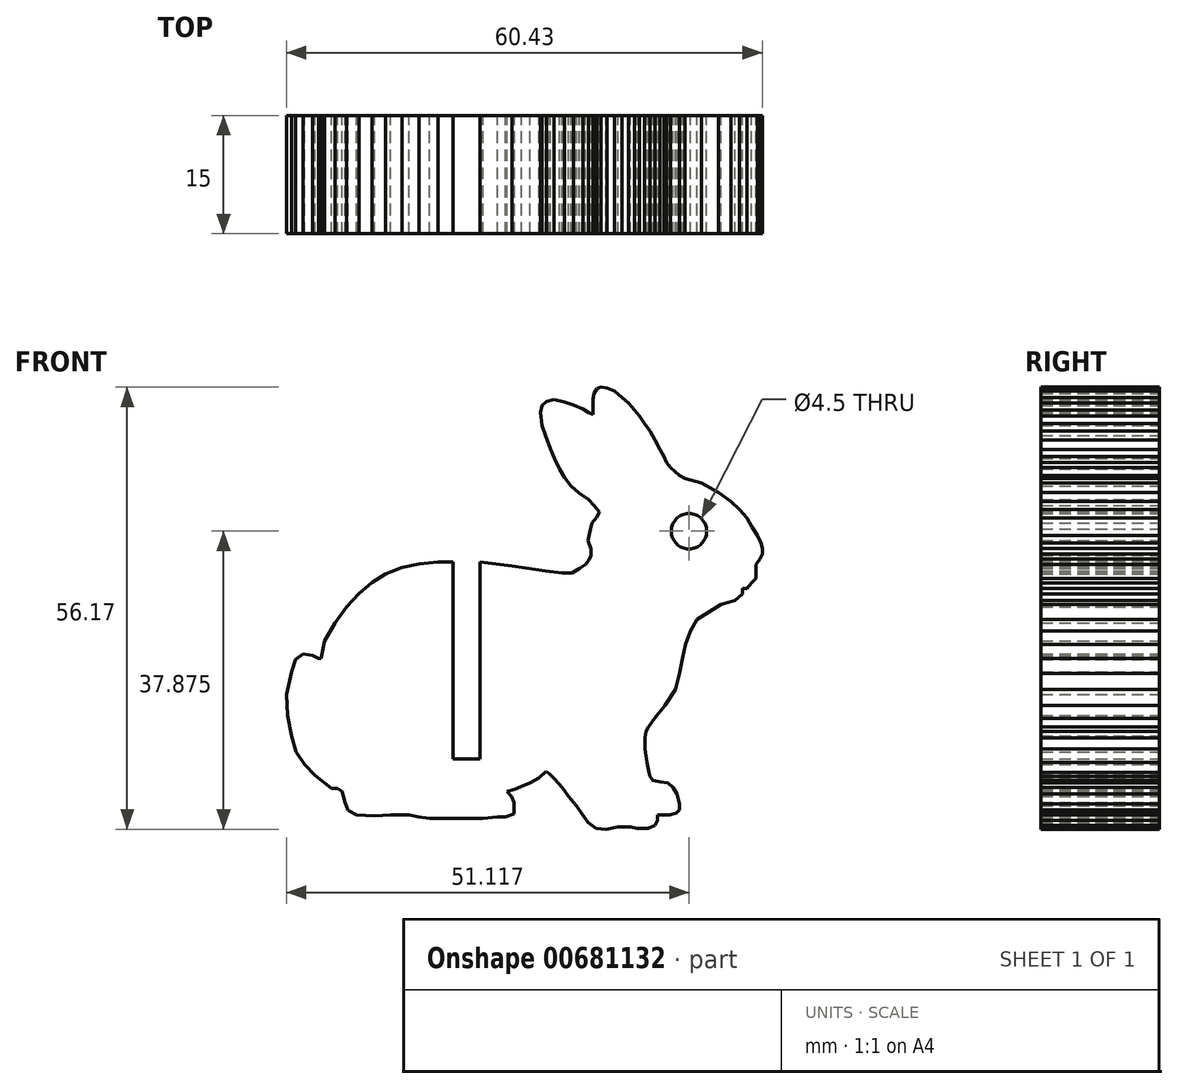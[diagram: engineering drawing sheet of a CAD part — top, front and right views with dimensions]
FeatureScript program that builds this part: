
annotation { "Feature Type Name" : "Feature", "Feature Type Description" : "" }
export const myFeature = defineFeature(function(context is Context, id is Id, definition is map)
    precondition{}
    {
        {
            var Q0;
            Q0=qCreatedBy(makeId("Front.planeOp"),FACE);
            var sketch = newSketch(context, id + "F0", { "sketchPlane" : qUnion([Q0])});
            skLineSegment(sketch, "E0", {"start": v(59.18, 31.9) * mm, "end": v(59.18, 31.2) * mm});
            skLineSegment(sketch, "E1", {"start": v(59.18, 31.2) * mm, "end": v(58.21, 30.37) * mm});
            skLineSegment(sketch, "E2", {"start": v(58.21, 30.37) * mm, "end": v(56.46, 29.85) * mm});
            skLineSegment(sketch, "E3", {"start": v(56.46, 29.85) * mm, "end": v(53.36, 27.96) * mm});
            skLineSegment(sketch, "E4", {"start": v(53.36, 27.96) * mm, "end": v(52.57, 26.52) * mm});
            skLineSegment(sketch, "E5", {"start": v(52.57, 26.52) * mm, "end": v(51.91, 24.8) * mm});
            skLineSegment(sketch, "E6", {"start": v(51.91, 24.8) * mm, "end": v(51.53, 22.99) * mm});
            skLineSegment(sketch, "E7", {"start": v(51.53, 22.99) * mm, "end": v(51.19, 21.11) * mm});
            skLineSegment(sketch, "E8", {"start": v(51.19, 21.11) * mm, "end": v(50.68, 19.1) * mm});
            skLineSegment(sketch, "E9", {"start": v(50.68, 19.1) * mm, "end": v(49.32, 17.01) * mm});
            skLineSegment(sketch, "E10", {"start": v(49.32, 17.01) * mm, "end": v(48.02, 15.39) * mm});
            skLineSegment(sketch, "E11", {"start": v(48.02, 15.39) * mm, "end": v(47.24, 14.33) * mm});
            skLineSegment(sketch, "E12", {"start": v(47.24, 14.33) * mm, "end": v(46.93, 13.71) * mm});
            skLineSegment(sketch, "E13", {"start": v(46.93, 13.71) * mm, "end": v(46.8, 12.88) * mm});
            skLineSegment(sketch, "E14", {"start": v(46.8, 12.88) * mm, "end": v(46.8, 11.49) * mm});
            skLineSegment(sketch, "E15", {"start": v(46.8, 11.49) * mm, "end": v(47.02, 9.82) * mm});
            skLineSegment(sketch, "E16", {"start": v(47.02, 9.82) * mm, "end": v(47.3, 8.54) * mm});
            skLineSegment(sketch, "E17", {"start": v(47.3, 8.54) * mm, "end": v(47.4, 8) * mm});
            skLineSegment(sketch, "E18", {"start": v(47.4, 8) * mm, "end": v(47.8, 7.53) * mm});
            skLineSegment(sketch, "E19", {"start": v(47.8, 7.53) * mm, "end": v(48.73, 7.33) * mm});
            skLineSegment(sketch, "E20", {"start": v(48.73, 7.33) * mm, "end": v(49.72, 7.17) * mm});
            skLineSegment(sketch, "E21", {"start": v(49.72, 7.17) * mm, "end": v(50.33, 6.61) * mm});
            skLineSegment(sketch, "E22", {"start": v(50.33, 6.61) * mm, "end": v(50.85, 5.82) * mm});
            skLineSegment(sketch, "E23", {"start": v(50.85, 5.82) * mm, "end": v(51.16, 4.55) * mm});
            skLineSegment(sketch, "E24", {"start": v(51.16, 4.55) * mm, "end": v(51.16, 3.77) * mm});
            skLineSegment(sketch, "E25", {"start": v(51.16, 3.77) * mm, "end": v(50.77, 3.37) * mm});
            skLineSegment(sketch, "E26", {"start": v(50.77, 3.37) * mm, "end": v(49.97, 3.1) * mm});
            skLineSegment(sketch, "E27", {"start": v(49.97, 3.1) * mm, "end": v(48.4, 3.1) * mm});
            skLineSegment(sketch, "E28", {"start": v(48.4, 3.1) * mm, "end": v(48.4, 2.43) * mm});
            skLineSegment(sketch, "E29", {"start": v(48.4, 2.43) * mm, "end": v(48.04, 1.82) * mm});
            skLineSegment(sketch, "E30", {"start": v(48.04, 1.82) * mm, "end": v(47.14, 1.41) * mm});
            skLineSegment(sketch, "E31", {"start": v(47.14, 1.41) * mm, "end": v(45.74, 1.41) * mm});
            skLineSegment(sketch, "E32", {"start": v(45.74, 1.41) * mm, "end": v(44.91, 1.62) * mm});
            skLineSegment(sketch, "E33", {"start": v(44.91, 1.62) * mm, "end": v(43.35, 1.62) * mm});
            skLineSegment(sketch, "E34", {"start": v(43.35, 1.62) * mm, "end": v(41.85, 1.3) * mm});
            skLineSegment(sketch, "E35", {"start": v(41.85, 1.3) * mm, "end": v(40.56, 1.41) * mm});
            skLineSegment(sketch, "E36", {"start": v(40.56, 1.41) * mm, "end": v(39.54, 2.2) * mm});
            skLineSegment(sketch, "E37", {"start": v(39.54, 2.2) * mm, "end": v(38.77, 3.29) * mm});
            skLineSegment(sketch, "E38", {"start": v(38.77, 3.29) * mm, "end": v(38.07, 4.3) * mm});
            skLineSegment(sketch, "E39", {"start": v(38.07, 4.3) * mm, "end": v(37.07, 5.46) * mm});
            skLineSegment(sketch, "E40", {"start": v(37.07, 5.46) * mm, "end": v(36.3, 6.57) * mm});
            skLineSegment(sketch, "E41", {"start": v(36.3, 6.57) * mm, "end": v(35.28, 7.7) * mm});
            skLineSegment(sketch, "E42", {"start": v(35.28, 7.7) * mm, "end": v(34.6, 8.39) * mm});
            skLineSegment(sketch, "E43", {"start": v(34.6, 8.39) * mm, "end": v(34.18, 8.68) * mm});
            skLineSegment(sketch, "E44", {"start": v(34.18, 8.68) * mm, "end": v(33.34, 7.84) * mm});
            skLineSegment(sketch, "E45", {"start": v(33.34, 7.84) * mm, "end": v(32.19, 7.18) * mm});
            skLineSegment(sketch, "E46", {"start": v(32.19, 7.18) * mm, "end": v(31.1, 6.72) * mm});
            skLineSegment(sketch, "E47", {"start": v(31.1, 6.72) * mm, "end": v(30.18, 6.39) * mm});
            skLineSegment(sketch, "E48", {"start": v(30.18, 6.39) * mm, "end": v(29.26, 6.12) * mm});
            skLineSegment(sketch, "E49", {"start": v(29.26, 6.12) * mm, "end": v(29.8, 5.51) * mm});
            skLineSegment(sketch, "E50", {"start": v(29.8, 5.51) * mm, "end": v(30.13, 4.73) * mm});
            skLineSegment(sketch, "E51", {"start": v(30.13, 4.73) * mm, "end": v(30.13, 4.07) * mm});
            skLineSegment(sketch, "E52", {"start": v(30.13, 4.07) * mm, "end": v(30.13, 3.51) * mm});
            skLineSegment(sketch, "E53", {"start": v(30.13, 3.51) * mm, "end": v(30.13, 3.29) * mm});
            skLineSegment(sketch, "E54", {"start": v(30.13, 3.29) * mm, "end": v(29.07, 2.88) * mm});
            skLineSegment(sketch, "E55", {"start": v(29.07, 2.88) * mm, "end": v(28.07, 2.88) * mm});
            skLineSegment(sketch, "E56", {"start": v(28.07, 2.88) * mm, "end": v(26.19, 2.66) * mm});
            skLineSegment(sketch, "E57", {"start": v(26.19, 2.66) * mm, "end": v(23.74, 2.66) * mm});
            skLineSegment(sketch, "E58", {"start": v(23.74, 2.66) * mm, "end": v(21.88, 2.66) * mm});
            skLineSegment(sketch, "E59", {"start": v(21.88, 2.66) * mm, "end": v(19.4, 2.66) * mm});
            skLineSegment(sketch, "E60", {"start": v(19.4, 2.66) * mm, "end": v(18, 2.88) * mm});
            skLineSegment(sketch, "E61", {"start": v(18, 2.88) * mm, "end": v(16.82, 3.14) * mm});
            skLineSegment(sketch, "E62", {"start": v(16.82, 3.14) * mm, "end": v(14.45, 3.14) * mm});
            skLineSegment(sketch, "E63", {"start": v(14.45, 3.14) * mm, "end": v(12.45, 3) * mm});
            skLineSegment(sketch, "E64", {"start": v(12.45, 3) * mm, "end": v(10.14, 3.13) * mm});
            skLineSegment(sketch, "E65", {"start": v(10.14, 3.13) * mm, "end": v(9.06, 3.73) * mm});
            skLineSegment(sketch, "E66", {"start": v(9.06, 3.73) * mm, "end": v(8.7, 4.73) * mm});
            skLineSegment(sketch, "E67", {"start": v(8.7, 4.73) * mm, "end": v(8.3, 6.14) * mm});
            skLineSegment(sketch, "E68", {"start": v(8.3, 6.14) * mm, "end": v(7.74, 6.47) * mm});
            skLineSegment(sketch, "E69", {"start": v(7.74, 6.47) * mm, "end": v(6.93, 6.47) * mm});
            skLineSegment(sketch, "E70", {"start": v(6.93, 6.47) * mm, "end": v(4.9, 8.14) * mm});
            skLineSegment(sketch, "E71", {"start": v(4.9, 8.14) * mm, "end": v(3.53, 9.54) * mm});
            skLineSegment(sketch, "E72", {"start": v(3.53, 9.54) * mm, "end": v(2.47, 11.15) * mm});
            skLineSegment(sketch, "E73", {"start": v(2.47, 11.15) * mm, "end": v(1.9, 13.14) * mm});
            skLineSegment(sketch, "E74", {"start": v(1.9, 13.14) * mm, "end": v(1.4, 15.75) * mm});
            skLineSegment(sketch, "E75", {"start": v(1.4, 15.75) * mm, "end": v(1.25, 18.43) * mm});
            skLineSegment(sketch, "E76", {"start": v(1.25, 18.43) * mm, "end": v(1.86, 21.3) * mm});
            skLineSegment(sketch, "E77", {"start": v(1.86, 21.3) * mm, "end": v(2.39, 22.87) * mm});
            skLineSegment(sketch, "E78", {"start": v(2.39, 22.87) * mm, "end": v(3.37, 23.56) * mm});
            skLineSegment(sketch, "E79", {"start": v(3.37, 23.56) * mm, "end": v(4.55, 23.4) * mm});
            skLineSegment(sketch, "E80", {"start": v(4.55, 23.4) * mm, "end": v(5.28, 22.99) * mm});
            skLineSegment(sketch, "E81", {"start": v(5.28, 22.99) * mm, "end": v(5.63, 22.99) * mm});
            skLineSegment(sketch, "E82", {"start": v(5.63, 22.99) * mm, "end": v(6.1, 25.22) * mm});
            skLineSegment(sketch, "E83", {"start": v(6.1, 25.22) * mm, "end": v(7.44, 27.53) * mm});
            skLineSegment(sketch, "E84", {"start": v(7.44, 27.53) * mm, "end": v(8.84, 29.53) * mm});
            skLineSegment(sketch, "E85", {"start": v(8.84, 29.53) * mm, "end": v(10.46, 31.27) * mm});
            skLineSegment(sketch, "E86", {"start": v(10.46, 31.27) * mm, "end": v(12.13, 32.66) * mm});
            skLineSegment(sketch, "E87", {"start": v(12.13, 32.66) * mm, "end": v(13.85, 33.74) * mm});
            skLineSegment(sketch, "E88", {"start": v(13.85, 33.74) * mm, "end": v(15.89, 34.56) * mm});
            skLineSegment(sketch, "E89", {"start": v(15.89, 34.56) * mm, "end": v(18.07, 35.02) * mm});
            skLineSegment(sketch, "E90", {"start": v(18.07, 35.02) * mm, "end": v(20.5, 35.25) * mm});
            skLineSegment(sketch, "E91", {"start": v(20.5, 35.25) * mm, "end": v(22.93, 35.25) * mm});
            skLineSegment(sketch, "E92", {"start": v(22.93, 35.25) * mm, "end": v(25.8, 35.25) * mm});
            skLineSegment(sketch, "E93", {"start": v(25.8, 35.25) * mm, "end": v(29.9, 34.74) * mm});
            skLineSegment(sketch, "E94", {"start": v(29.9, 34.74) * mm, "end": v(31.58, 34.5) * mm});
            skLineSegment(sketch, "E95", {"start": v(31.58, 34.5) * mm, "end": v(34.17, 34.11) * mm});
            skLineSegment(sketch, "E96", {"start": v(34.17, 34.11) * mm, "end": v(36.24, 33.84) * mm});
            skLineSegment(sketch, "E97", {"start": v(36.24, 33.84) * mm, "end": v(37.5, 33.84) * mm});
            skLineSegment(sketch, "E98", {"start": v(37.5, 33.84) * mm, "end": v(38.48, 34.41) * mm});
            skLineSegment(sketch, "E99", {"start": v(38.48, 34.41) * mm, "end": v(39.21, 34.95) * mm});
            skLineSegment(sketch, "E100", {"start": v(39.21, 34.95) * mm, "end": v(39.69, 35.51) * mm});
            skLineSegment(sketch, "E101", {"start": v(39.69, 35.51) * mm, "end": v(39.94, 36.1) * mm});
            skLineSegment(sketch, "E102", {"start": v(39.94, 36.1) * mm, "end": v(39.94, 36.93) * mm});
            skLineSegment(sketch, "E103", {"start": v(39.94, 36.93) * mm, "end": v(39.54, 38.02) * mm});
            skLineSegment(sketch, "E104", {"start": v(39.54, 38.02) * mm, "end": v(39.83, 39.44) * mm});
            skLineSegment(sketch, "E105", {"start": v(39.83, 39.44) * mm, "end": v(40.08, 40.2) * mm});
            skLineSegment(sketch, "E106", {"start": v(40.08, 40.2) * mm, "end": v(40.6, 40.94) * mm});
            skLineSegment(sketch, "E107", {"start": v(40.6, 40.94) * mm, "end": v(41, 41.61) * mm});
            skLineSegment(sketch, "E108", {"start": v(41, 41.61) * mm, "end": v(40.3, 42.4) * mm});
            skLineSegment(sketch, "E109", {"start": v(40.3, 42.4) * mm, "end": v(39.57, 43.22) * mm});
            skLineSegment(sketch, "E110", {"start": v(39.57, 43.22) * mm, "end": v(38.4, 44.03) * mm});
            skLineSegment(sketch, "E111", {"start": v(38.4, 44.03) * mm, "end": v(37.38, 44.92) * mm});
            skLineSegment(sketch, "E112", {"start": v(37.38, 44.92) * mm, "end": v(36.53, 45.97) * mm});
            skLineSegment(sketch, "E113", {"start": v(36.53, 45.97) * mm, "end": v(35.9, 47.05) * mm});
            skLineSegment(sketch, "E114", {"start": v(35.9, 47.05) * mm, "end": v(35.26, 48.39) * mm});
            skLineSegment(sketch, "E115", {"start": v(35.26, 48.39) * mm, "end": v(34.77, 49.59) * mm});
            skLineSegment(sketch, "E116", {"start": v(34.77, 49.59) * mm, "end": v(34.17, 51.34) * mm});
            skLineSegment(sketch, "E117", {"start": v(34.17, 51.34) * mm, "end": v(33.68, 52.6) * mm});
            skLineSegment(sketch, "E118", {"start": v(33.68, 52.6) * mm, "end": v(33.5, 54.23) * mm});
            skLineSegment(sketch, "E119", {"start": v(33.5, 54.23) * mm, "end": v(33.67, 55.17) * mm});
            skLineSegment(sketch, "E120", {"start": v(33.67, 55.17) * mm, "end": v(34.28, 55.63) * mm});
            skLineSegment(sketch, "E121", {"start": v(34.28, 55.63) * mm, "end": v(35.19, 55.89) * mm});
            skLineSegment(sketch, "E122", {"start": v(35.19, 55.89) * mm, "end": v(36.57, 55.6) * mm});
            skLineSegment(sketch, "E123", {"start": v(36.57, 55.6) * mm, "end": v(37.7, 55.18) * mm});
            skLineSegment(sketch, "E124", {"start": v(37.7, 55.18) * mm, "end": v(38.87, 54.67) * mm});
            skLineSegment(sketch, "E125", {"start": v(38.87, 54.67) * mm, "end": v(39.6, 54.27) * mm});
            skLineSegment(sketch, "E126", {"start": v(39.6, 54.27) * mm, "end": v(40.2, 53.98) * mm});
            skLineSegment(sketch, "E127", {"start": v(40.2, 53.98) * mm, "end": v(40.2, 55.95) * mm});
            skLineSegment(sketch, "E128", {"start": v(40.2, 55.95) * mm, "end": v(40.3, 56.68) * mm});
            skLineSegment(sketch, "E129", {"start": v(40.3, 56.68) * mm, "end": v(40.7, 57.32) * mm});
            skLineSegment(sketch, "E130", {"start": v(40.7, 57.32) * mm, "end": v(41.2, 57.47) * mm});
            skLineSegment(sketch, "E131", {"start": v(41.2, 57.47) * mm, "end": v(41.98, 57.38) * mm});
            skLineSegment(sketch, "E132", {"start": v(41.98, 57.38) * mm, "end": v(42.9, 56.96) * mm});
            skLineSegment(sketch, "E133", {"start": v(42.9, 56.96) * mm, "end": v(43.88, 56.18) * mm});
            skLineSegment(sketch, "E134", {"start": v(43.88, 56.18) * mm, "end": v(44.66, 55.47) * mm});
            skLineSegment(sketch, "E135", {"start": v(44.66, 55.47) * mm, "end": v(45.46, 54.57) * mm});
            skLineSegment(sketch, "E136", {"start": v(45.46, 54.57) * mm, "end": v(46.07, 53.8) * mm});
            skLineSegment(sketch, "E137", {"start": v(46.07, 53.8) * mm, "end": v(46.74, 52.83) * mm});
            skLineSegment(sketch, "E138", {"start": v(46.74, 52.83) * mm, "end": v(47.4, 51.92) * mm});
            skLineSegment(sketch, "E139", {"start": v(47.4, 51.92) * mm, "end": v(48.07, 50.76) * mm});
            skLineSegment(sketch, "E140", {"start": v(48.07, 50.76) * mm, "end": v(48.69, 49.58) * mm});
            skLineSegment(sketch, "E141", {"start": v(48.69, 49.58) * mm, "end": v(49.16, 48.64) * mm});
            skLineSegment(sketch, "E142", {"start": v(49.16, 48.64) * mm, "end": v(49.5, 47.92) * mm});
            skLineSegment(sketch, "E143", {"start": v(49.5, 47.92) * mm, "end": v(50.03, 47.25) * mm});
            skLineSegment(sketch, "E144", {"start": v(50.03, 47.25) * mm, "end": v(51.16, 46.28) * mm});
            skLineSegment(sketch, "E145", {"start": v(51.16, 46.28) * mm, "end": v(51.87, 45.89) * mm});
            skLineSegment(sketch, "E146", {"start": v(51.87, 45.89) * mm, "end": v(53.94, 45.3) * mm});
            skLineSegment(sketch, "E147", {"start": v(53.94, 45.3) * mm, "end": v(56.13, 44.1) * mm});
            skLineSegment(sketch, "E148", {"start": v(56.13, 44.1) * mm, "end": v(57.69, 42.96) * mm});
            skLineSegment(sketch, "E149", {"start": v(57.69, 42.96) * mm, "end": v(58.76, 41.92) * mm});
            skLineSegment(sketch, "E150", {"start": v(58.76, 41.92) * mm, "end": v(59.7, 40.84) * mm});
            skLineSegment(sketch, "E151", {"start": v(59.7, 40.84) * mm, "end": v(60.39, 39.73) * mm});
            skLineSegment(sketch, "E152", {"start": v(60.39, 39.73) * mm, "end": v(61.06, 38.64) * mm});
            skLineSegment(sketch, "E153", {"start": v(61.06, 38.64) * mm, "end": v(61.48, 37.65) * mm});
            skLineSegment(sketch, "E154", {"start": v(61.48, 37.65) * mm, "end": v(61.68, 36.96) * mm});
            skLineSegment(sketch, "E155", {"start": v(61.68, 36.96) * mm, "end": v(61.68, 36.3) * mm});
            skLineSegment(sketch, "E156", {"start": v(61.68, 36.3) * mm, "end": v(61.36, 35.64) * mm});
            skLineSegment(sketch, "E157", {"start": v(61.36, 35.64) * mm, "end": v(60.9, 34.95) * mm});
            skLineSegment(sketch, "E158", {"start": v(60.9, 34.95) * mm, "end": v(60.9, 33.94) * mm});
            skLineSegment(sketch, "E159", {"start": v(60.9, 33.94) * mm, "end": v(60.9, 33.16) * mm});
            skLineSegment(sketch, "E160", {"start": v(60.9, 33.16) * mm, "end": v(60.3, 32.6) * mm});
            skLineSegment(sketch, "E161", {"start": v(60.3, 32.6) * mm, "end": v(59.74, 31.88) * mm});
            skLineSegment(sketch, "E162", {"start": v(59.74, 31.88) * mm, "end": v(59.18, 31.9) * mm});
            skCircle(sketch, "E163", {"center": v(52.37, 39.17) * mm, "radius": 2.25 * mm});
            skSolve(sketch);
        }
        {
            var Q0;
            Q0=makeQuery(id+"F0.imprint","IMPRINT",FACE,{"disambiguationData":[TD([[makeQuery(id+"F0.imprint","IMPRINT",EDGE,{"derivedFrom":sQuery(id+"F0.wireOp",EDGE,"E0")}),-1.0]])]});
            extrude(context, id + "F1", {"entities" : qUnion([Q0]), "depth" : 3 * mm, "offsetDistance" : 25 * mm});
        }
        {
            var Q0;
            Q0=makeQuery(id+"F1.opExtrude","CAP_FACE",FACE,{"disambiguationData":[OSD([sQuery(id+"F0.wireOp",EDGE,"E0"),sQuery(id+"F0.wireOp",EDGE,"E1"),sQuery(id+"F0.wireOp",EDGE,"E2"),sQuery(id+"F0.wireOp",EDGE,"E3"),sQuery(id+"F0.wireOp",EDGE,"E4"),sQuery(id+"F0.wireOp",EDGE,"E5"),sQuery(id+"F0.wireOp",EDGE,"E6"),sQuery(id+"F0.wireOp",EDGE,"E7"),sQuery(id+"F0.wireOp",EDGE,"E8"),sQuery(id+"F0.wireOp",EDGE,"E9"),sQuery(id+"F0.wireOp",EDGE,"E10"),sQuery(id+"F0.wireOp",EDGE,"E11"),sQuery(id+"F0.wireOp",EDGE,"E12"),sQuery(id+"F0.wireOp",EDGE,"E13"),sQuery(id+"F0.wireOp",EDGE,"E14"),sQuery(id+"F0.wireOp",EDGE,"E15"),sQuery(id+"F0.wireOp",EDGE,"E16"),sQuery(id+"F0.wireOp",EDGE,"E17"),sQuery(id+"F0.wireOp",EDGE,"E18"),sQuery(id+"F0.wireOp",EDGE,"E19"),sQuery(id+"F0.wireOp",EDGE,"E20"),sQuery(id+"F0.wireOp",EDGE,"E21"),sQuery(id+"F0.wireOp",EDGE,"E22"),sQuery(id+"F0.wireOp",EDGE,"E23"),sQuery(id+"F0.wireOp",EDGE,"E24"),sQuery(id+"F0.wireOp",EDGE,"E25"),sQuery(id+"F0.wireOp",EDGE,"E26"),sQuery(id+"F0.wireOp",EDGE,"E27"),sQuery(id+"F0.wireOp",EDGE,"E28"),sQuery(id+"F0.wireOp",EDGE,"E29"),sQuery(id+"F0.wireOp",EDGE,"E30"),sQuery(id+"F0.wireOp",EDGE,"E31"),sQuery(id+"F0.wireOp",EDGE,"E32"),sQuery(id+"F0.wireOp",EDGE,"E33"),sQuery(id+"F0.wireOp",EDGE,"E34"),sQuery(id+"F0.wireOp",EDGE,"E35"),sQuery(id+"F0.wireOp",EDGE,"E36"),sQuery(id+"F0.wireOp",EDGE,"E37"),sQuery(id+"F0.wireOp",EDGE,"E38"),sQuery(id+"F0.wireOp",EDGE,"E39"),sQuery(id+"F0.wireOp",EDGE,"E40"),sQuery(id+"F0.wireOp",EDGE,"E41"),sQuery(id+"F0.wireOp",EDGE,"E42"),sQuery(id+"F0.wireOp",EDGE,"E43"),sQuery(id+"F0.wireOp",EDGE,"E44"),sQuery(id+"F0.wireOp",EDGE,"E45"),sQuery(id+"F0.wireOp",EDGE,"E46"),sQuery(id+"F0.wireOp",EDGE,"E47"),sQuery(id+"F0.wireOp",EDGE,"E48"),sQuery(id+"F0.wireOp",EDGE,"E49"),sQuery(id+"F0.wireOp",EDGE,"E50"),sQuery(id+"F0.wireOp",EDGE,"E51"),sQuery(id+"F0.wireOp",EDGE,"E52"),sQuery(id+"F0.wireOp",EDGE,"E53"),sQuery(id+"F0.wireOp",EDGE,"E54"),sQuery(id+"F0.wireOp",EDGE,"E55"),sQuery(id+"F0.wireOp",EDGE,"E56"),sQuery(id+"F0.wireOp",EDGE,"E57"),sQuery(id+"F0.wireOp",EDGE,"E58"),sQuery(id+"F0.wireOp",EDGE,"E59"),sQuery(id+"F0.wireOp",EDGE,"E60"),sQuery(id+"F0.wireOp",EDGE,"E61"),sQuery(id+"F0.wireOp",EDGE,"E62"),sQuery(id+"F0.wireOp",EDGE,"E63"),sQuery(id+"F0.wireOp",EDGE,"E64"),sQuery(id+"F0.wireOp",EDGE,"E65"),sQuery(id+"F0.wireOp",EDGE,"E66"),sQuery(id+"F0.wireOp",EDGE,"E67"),sQuery(id+"F0.wireOp",EDGE,"E68"),sQuery(id+"F0.wireOp",EDGE,"E69"),sQuery(id+"F0.wireOp",EDGE,"E70"),sQuery(id+"F0.wireOp",EDGE,"E71"),sQuery(id+"F0.wireOp",EDGE,"E72"),sQuery(id+"F0.wireOp",EDGE,"E73"),sQuery(id+"F0.wireOp",EDGE,"E74"),sQuery(id+"F0.wireOp",EDGE,"E75"),sQuery(id+"F0.wireOp",EDGE,"E76"),sQuery(id+"F0.wireOp",EDGE,"E77"),sQuery(id+"F0.wireOp",EDGE,"E78"),sQuery(id+"F0.wireOp",EDGE,"E79"),sQuery(id+"F0.wireOp",EDGE,"E80"),sQuery(id+"F0.wireOp",EDGE,"E81"),sQuery(id+"F0.wireOp",EDGE,"E82"),sQuery(id+"F0.wireOp",EDGE,"E83"),sQuery(id+"F0.wireOp",EDGE,"E84"),sQuery(id+"F0.wireOp",EDGE,"E85"),sQuery(id+"F0.wireOp",EDGE,"E86"),sQuery(id+"F0.wireOp",EDGE,"E87"),sQuery(id+"F0.wireOp",EDGE,"E88"),sQuery(id+"F0.wireOp",EDGE,"E89"),sQuery(id+"F0.wireOp",EDGE,"E90"),sQuery(id+"F0.wireOp",EDGE,"E91"),sQuery(id+"F0.wireOp",EDGE,"E92"),sQuery(id+"F0.wireOp",EDGE,"E93"),sQuery(id+"F0.wireOp",EDGE,"E94"),sQuery(id+"F0.wireOp",EDGE,"E95"),sQuery(id+"F0.wireOp",EDGE,"E96"),sQuery(id+"F0.wireOp",EDGE,"E97"),sQuery(id+"F0.wireOp",EDGE,"E98"),sQuery(id+"F0.wireOp",EDGE,"E99"),sQuery(id+"F0.wireOp",EDGE,"E100"),sQuery(id+"F0.wireOp",EDGE,"E101"),sQuery(id+"F0.wireOp",EDGE,"E102"),sQuery(id+"F0.wireOp",EDGE,"E103"),sQuery(id+"F0.wireOp",EDGE,"E104"),sQuery(id+"F0.wireOp",EDGE,"E105"),sQuery(id+"F0.wireOp",EDGE,"E106"),sQuery(id+"F0.wireOp",EDGE,"E107"),sQuery(id+"F0.wireOp",EDGE,"E108"),sQuery(id+"F0.wireOp",EDGE,"E109"),sQuery(id+"F0.wireOp",EDGE,"E110"),sQuery(id+"F0.wireOp",EDGE,"E111"),sQuery(id+"F0.wireOp",EDGE,"E112"),sQuery(id+"F0.wireOp",EDGE,"E113"),sQuery(id+"F0.wireOp",EDGE,"E114"),sQuery(id+"F0.wireOp",EDGE,"E115"),sQuery(id+"F0.wireOp",EDGE,"E116"),sQuery(id+"F0.wireOp",EDGE,"E117"),sQuery(id+"F0.wireOp",EDGE,"E118"),sQuery(id+"F0.wireOp",EDGE,"E119"),sQuery(id+"F0.wireOp",EDGE,"E120"),sQuery(id+"F0.wireOp",EDGE,"E121"),sQuery(id+"F0.wireOp",EDGE,"E122"),sQuery(id+"F0.wireOp",EDGE,"E123"),sQuery(id+"F0.wireOp",EDGE,"E124"),sQuery(id+"F0.wireOp",EDGE,"E125"),sQuery(id+"F0.wireOp",EDGE,"E126"),sQuery(id+"F0.wireOp",EDGE,"E127"),sQuery(id+"F0.wireOp",EDGE,"E128"),sQuery(id+"F0.wireOp",EDGE,"E129"),sQuery(id+"F0.wireOp",EDGE,"E130"),sQuery(id+"F0.wireOp",EDGE,"E131"),sQuery(id+"F0.wireOp",EDGE,"E132"),sQuery(id+"F0.wireOp",EDGE,"E133"),sQuery(id+"F0.wireOp",EDGE,"E134"),sQuery(id+"F0.wireOp",EDGE,"E135"),sQuery(id+"F0.wireOp",EDGE,"E136"),sQuery(id+"F0.wireOp",EDGE,"E137"),sQuery(id+"F0.wireOp",EDGE,"E138"),sQuery(id+"F0.wireOp",EDGE,"E139"),sQuery(id+"F0.wireOp",EDGE,"E140"),sQuery(id+"F0.wireOp",EDGE,"E141"),sQuery(id+"F0.wireOp",EDGE,"E142"),sQuery(id+"F0.wireOp",EDGE,"E143"),sQuery(id+"F0.wireOp",EDGE,"E144"),sQuery(id+"F0.wireOp",EDGE,"E145"),sQuery(id+"F0.wireOp",EDGE,"E146"),sQuery(id+"F0.wireOp",EDGE,"E147"),sQuery(id+"F0.wireOp",EDGE,"E148"),sQuery(id+"F0.wireOp",EDGE,"E149"),sQuery(id+"F0.wireOp",EDGE,"E150"),sQuery(id+"F0.wireOp",EDGE,"E151"),sQuery(id+"F0.wireOp",EDGE,"E152"),sQuery(id+"F0.wireOp",EDGE,"E153"),sQuery(id+"F0.wireOp",EDGE,"E154"),sQuery(id+"F0.wireOp",EDGE,"E155"),sQuery(id+"F0.wireOp",EDGE,"E156"),sQuery(id+"F0.wireOp",EDGE,"E157"),sQuery(id+"F0.wireOp",EDGE,"E158"),sQuery(id+"F0.wireOp",EDGE,"E159"),sQuery(id+"F0.wireOp",EDGE,"E160"),sQuery(id+"F0.wireOp",EDGE,"E161"),sQuery(id+"F0.wireOp",EDGE,"E162"),sQuery(id+"F0.wireOp",EDGE,"E163")])],"isStart":false});
            extrude(context, id + "F2", {"entities" : qUnion([Q0]), "operationType" : NewBodyOperationType.ADD, "depth" : 12 * mm, "offsetDistance" : 25 * mm});
        }
        {
            var Q0;
            {var subQ0=sQuery(id+"F0.wireOp",EDGE,"E92");var subQ1=sQuery(id+"F0.wireOp",EDGE,"E91");Q0=makeQuery(id+"F2.boolean.opBoolean","MERGE",FACE,{"derivedFrom":[makeQuery(id+"F1.opExtrude","SWEPT_FACE",FACE,{"disambiguationData":[OSD([subQ1,subQ0])]}),makeQuery(id+"F2.opExtrude","SWEPT_FACE",FACE,{"disambiguationData":[OSD([subQ1,subQ0])]})]});}
            extrude(context, id + "F3", {"entities" : qUnion([Q0]), "operationType" : NewBodyOperationType.REMOVE, "oppositeDirection" : true, "depth" : 25 * mm, "offsetDistance" : 25 * mm});
        }
        {
            var Q0;
            Q0=makeQuery(id+"F3.boolean.opBoolean","COPY",FACE,{"derivedFrom":makeQuery(id+"F3.opExtrude","SWEPT_FACE",FACE,{"disambiguationData":[OSD([sQuery(id+"F0.wireOp",EDGE,"E90"),sQuery(id+"F0.wireOp",EDGE,"E91")])]})});
            extrude(context, id + "F4", {"entities" : qUnion([Q0]), "operationType" : NewBodyOperationType.ADD, "depth" : 1.9 * mm, "offsetDistance" : 25 * mm});
        }
        {
            var Q0;
            {var subQ0=sQuery(id+"F0.wireOp",EDGE,"E91");var subQ1=sQuery(id+"F0.wireOp",EDGE,"E90");Q0=makeQuery(id+"F4.boolean.opBoolean","MERGE",FACE,{"derivedFrom":[makeQuery(id+"F2.opExtrude","CAP_FACE",FACE,{"disambiguationData":[OSD([sQuery(id+"F0.wireOp",EDGE,"E0"),sQuery(id+"F0.wireOp",EDGE,"E1"),sQuery(id+"F0.wireOp",EDGE,"E2"),sQuery(id+"F0.wireOp",EDGE,"E3"),sQuery(id+"F0.wireOp",EDGE,"E4"),sQuery(id+"F0.wireOp",EDGE,"E5"),sQuery(id+"F0.wireOp",EDGE,"E6"),sQuery(id+"F0.wireOp",EDGE,"E7"),sQuery(id+"F0.wireOp",EDGE,"E8"),sQuery(id+"F0.wireOp",EDGE,"E9"),sQuery(id+"F0.wireOp",EDGE,"E10"),sQuery(id+"F0.wireOp",EDGE,"E11"),sQuery(id+"F0.wireOp",EDGE,"E12"),sQuery(id+"F0.wireOp",EDGE,"E13"),sQuery(id+"F0.wireOp",EDGE,"E14"),sQuery(id+"F0.wireOp",EDGE,"E15"),sQuery(id+"F0.wireOp",EDGE,"E16"),sQuery(id+"F0.wireOp",EDGE,"E17"),sQuery(id+"F0.wireOp",EDGE,"E18"),sQuery(id+"F0.wireOp",EDGE,"E19"),sQuery(id+"F0.wireOp",EDGE,"E20"),sQuery(id+"F0.wireOp",EDGE,"E21"),sQuery(id+"F0.wireOp",EDGE,"E22"),sQuery(id+"F0.wireOp",EDGE,"E23"),sQuery(id+"F0.wireOp",EDGE,"E24"),sQuery(id+"F0.wireOp",EDGE,"E25"),sQuery(id+"F0.wireOp",EDGE,"E26"),sQuery(id+"F0.wireOp",EDGE,"E27"),sQuery(id+"F0.wireOp",EDGE,"E28"),sQuery(id+"F0.wireOp",EDGE,"E29"),sQuery(id+"F0.wireOp",EDGE,"E30"),sQuery(id+"F0.wireOp",EDGE,"E31"),sQuery(id+"F0.wireOp",EDGE,"E32"),sQuery(id+"F0.wireOp",EDGE,"E33"),sQuery(id+"F0.wireOp",EDGE,"E34"),sQuery(id+"F0.wireOp",EDGE,"E35"),sQuery(id+"F0.wireOp",EDGE,"E36"),sQuery(id+"F0.wireOp",EDGE,"E37"),sQuery(id+"F0.wireOp",EDGE,"E38"),sQuery(id+"F0.wireOp",EDGE,"E39"),sQuery(id+"F0.wireOp",EDGE,"E40"),sQuery(id+"F0.wireOp",EDGE,"E41"),sQuery(id+"F0.wireOp",EDGE,"E42"),sQuery(id+"F0.wireOp",EDGE,"E43"),sQuery(id+"F0.wireOp",EDGE,"E44"),sQuery(id+"F0.wireOp",EDGE,"E45"),sQuery(id+"F0.wireOp",EDGE,"E46"),sQuery(id+"F0.wireOp",EDGE,"E47"),sQuery(id+"F0.wireOp",EDGE,"E48"),sQuery(id+"F0.wireOp",EDGE,"E49"),sQuery(id+"F0.wireOp",EDGE,"E50"),sQuery(id+"F0.wireOp",EDGE,"E51"),sQuery(id+"F0.wireOp",EDGE,"E52"),sQuery(id+"F0.wireOp",EDGE,"E53"),sQuery(id+"F0.wireOp",EDGE,"E54"),sQuery(id+"F0.wireOp",EDGE,"E55"),sQuery(id+"F0.wireOp",EDGE,"E56"),sQuery(id+"F0.wireOp",EDGE,"E57"),sQuery(id+"F0.wireOp",EDGE,"E58"),sQuery(id+"F0.wireOp",EDGE,"E59"),sQuery(id+"F0.wireOp",EDGE,"E60"),sQuery(id+"F0.wireOp",EDGE,"E61"),sQuery(id+"F0.wireOp",EDGE,"E62"),sQuery(id+"F0.wireOp",EDGE,"E63"),sQuery(id+"F0.wireOp",EDGE,"E64"),sQuery(id+"F0.wireOp",EDGE,"E65"),sQuery(id+"F0.wireOp",EDGE,"E66"),sQuery(id+"F0.wireOp",EDGE,"E67"),sQuery(id+"F0.wireOp",EDGE,"E68"),sQuery(id+"F0.wireOp",EDGE,"E69"),sQuery(id+"F0.wireOp",EDGE,"E70"),sQuery(id+"F0.wireOp",EDGE,"E71"),sQuery(id+"F0.wireOp",EDGE,"E72"),sQuery(id+"F0.wireOp",EDGE,"E73"),sQuery(id+"F0.wireOp",EDGE,"E74"),sQuery(id+"F0.wireOp",EDGE,"E75"),sQuery(id+"F0.wireOp",EDGE,"E76"),sQuery(id+"F0.wireOp",EDGE,"E77"),sQuery(id+"F0.wireOp",EDGE,"E78"),sQuery(id+"F0.wireOp",EDGE,"E79"),sQuery(id+"F0.wireOp",EDGE,"E80"),sQuery(id+"F0.wireOp",EDGE,"E81"),sQuery(id+"F0.wireOp",EDGE,"E82"),sQuery(id+"F0.wireOp",EDGE,"E83"),sQuery(id+"F0.wireOp",EDGE,"E84"),sQuery(id+"F0.wireOp",EDGE,"E85"),sQuery(id+"F0.wireOp",EDGE,"E86"),sQuery(id+"F0.wireOp",EDGE,"E87"),sQuery(id+"F0.wireOp",EDGE,"E88"),sQuery(id+"F0.wireOp",EDGE,"E89"),subQ1,subQ0,sQuery(id+"F0.wireOp",EDGE,"E92"),sQuery(id+"F0.wireOp",EDGE,"E93"),sQuery(id+"F0.wireOp",EDGE,"E94"),sQuery(id+"F0.wireOp",EDGE,"E95"),sQuery(id+"F0.wireOp",EDGE,"E96"),sQuery(id+"F0.wireOp",EDGE,"E97"),sQuery(id+"F0.wireOp",EDGE,"E98"),sQuery(id+"F0.wireOp",EDGE,"E99"),sQuery(id+"F0.wireOp",EDGE,"E100"),sQuery(id+"F0.wireOp",EDGE,"E101"),sQuery(id+"F0.wireOp",EDGE,"E102"),sQuery(id+"F0.wireOp",EDGE,"E103"),sQuery(id+"F0.wireOp",EDGE,"E104"),sQuery(id+"F0.wireOp",EDGE,"E105"),sQuery(id+"F0.wireOp",EDGE,"E106"),sQuery(id+"F0.wireOp",EDGE,"E107"),sQuery(id+"F0.wireOp",EDGE,"E108"),sQuery(id+"F0.wireOp",EDGE,"E109"),sQuery(id+"F0.wireOp",EDGE,"E110"),sQuery(id+"F0.wireOp",EDGE,"E111"),sQuery(id+"F0.wireOp",EDGE,"E112"),sQuery(id+"F0.wireOp",EDGE,"E113"),sQuery(id+"F0.wireOp",EDGE,"E114"),sQuery(id+"F0.wireOp",EDGE,"E115"),sQuery(id+"F0.wireOp",EDGE,"E116"),sQuery(id+"F0.wireOp",EDGE,"E117"),sQuery(id+"F0.wireOp",EDGE,"E118"),sQuery(id+"F0.wireOp",EDGE,"E119"),sQuery(id+"F0.wireOp",EDGE,"E120"),sQuery(id+"F0.wireOp",EDGE,"E121"),sQuery(id+"F0.wireOp",EDGE,"E122"),sQuery(id+"F0.wireOp",EDGE,"E123"),sQuery(id+"F0.wireOp",EDGE,"E124"),sQuery(id+"F0.wireOp",EDGE,"E125"),sQuery(id+"F0.wireOp",EDGE,"E126"),sQuery(id+"F0.wireOp",EDGE,"E127"),sQuery(id+"F0.wireOp",EDGE,"E128"),sQuery(id+"F0.wireOp",EDGE,"E129"),sQuery(id+"F0.wireOp",EDGE,"E130"),sQuery(id+"F0.wireOp",EDGE,"E131"),sQuery(id+"F0.wireOp",EDGE,"E132"),sQuery(id+"F0.wireOp",EDGE,"E133"),sQuery(id+"F0.wireOp",EDGE,"E134"),sQuery(id+"F0.wireOp",EDGE,"E135"),sQuery(id+"F0.wireOp",EDGE,"E136"),sQuery(id+"F0.wireOp",EDGE,"E137"),sQuery(id+"F0.wireOp",EDGE,"E138"),sQuery(id+"F0.wireOp",EDGE,"E139"),sQuery(id+"F0.wireOp",EDGE,"E140"),sQuery(id+"F0.wireOp",EDGE,"E141"),sQuery(id+"F0.wireOp",EDGE,"E142"),sQuery(id+"F0.wireOp",EDGE,"E143"),sQuery(id+"F0.wireOp",EDGE,"E144"),sQuery(id+"F0.wireOp",EDGE,"E145"),sQuery(id+"F0.wireOp",EDGE,"E146"),sQuery(id+"F0.wireOp",EDGE,"E147"),sQuery(id+"F0.wireOp",EDGE,"E148"),sQuery(id+"F0.wireOp",EDGE,"E149"),sQuery(id+"F0.wireOp",EDGE,"E150"),sQuery(id+"F0.wireOp",EDGE,"E151"),sQuery(id+"F0.wireOp",EDGE,"E152"),sQuery(id+"F0.wireOp",EDGE,"E153"),sQuery(id+"F0.wireOp",EDGE,"E154"),sQuery(id+"F0.wireOp",EDGE,"E155"),sQuery(id+"F0.wireOp",EDGE,"E156"),sQuery(id+"F0.wireOp",EDGE,"E157"),sQuery(id+"F0.wireOp",EDGE,"E158"),sQuery(id+"F0.wireOp",EDGE,"E159"),sQuery(id+"F0.wireOp",EDGE,"E160"),sQuery(id+"F0.wireOp",EDGE,"E161"),sQuery(id+"F0.wireOp",EDGE,"E162"),sQuery(id+"F0.wireOp",EDGE,"E163")])],"isStart":false}),makeQuery(id+"F4.opExtrude","SWEPT_FACE",FACE,{"disambiguationData":[OSD([subQ1,subQ0]),TDD([makeQuery(id+"F3.boolean.opBoolean","COPY",EDGE,{"derivedFrom":makeQuery(id+"F3.opExtrude","SWEPT_EDGE",EDGE,{"disambiguationData":[OSD([subQ1,subQ0]),TDD([makeQuery(id+"F2.opExtrude","CAP_VERTEX",VERTEX,{"disambiguationData":[OSD([subQ1,subQ0])],"isStart":false})])]})})])]})]});}
            var sketch = newSketch(context, id + "F5", { "sketchPlane" : qUnion([Q0])});
            skCircle(sketch, "E164", {"center": v(41.8, 54.4) * mm, "radius": 1.03 * mm});
            skSolve(sketch);
        }
        {
            var Q0;
            Q0 = qSketchRegion(id + "F5", true);
            extrude(context, id + "F6", {"entities" : qUnion([Q0]), "operationType" : NewBodyOperationType.ADD, "oppositeDirection" : true, "depth" : 2 * mm, "offsetDistance" : 25 * mm});
        }
    });
